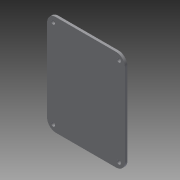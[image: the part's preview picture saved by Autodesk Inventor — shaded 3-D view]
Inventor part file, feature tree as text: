
AUTODESK INVENTOR PART (.ipt)
format: ipt  version: 2014 (Build 180170000, 170)  size: 131,584 bytes
history: native  units: mm
features: extrude x2, sketch x2, chamfer x1
ambient origin geometry x8: Origin, YZ Plane, XZ Plane, XY Plane, X Axis, Y Axis, Z Axis, Center Point
bodies: Solid1 (feature_tree)
feature tree (5):
  extrude  "Extrusion1"  Depth=5.0mm TaperAngle=0.0deg
  extrude  "Extrusion2"  Depth=5.0mm TaperAngle=45.0deg
  chamfer  "Chamfer1"  Distance=12.0mm
  sketch  "Sketch1"  dims[d0=2.2mm d1=0.0mm]
  sketch  "Sketch2"  dims[d5=2.5mm d6=6.0mm d7=2.5mm d8=6.0mm d9=2.5mm d10=6.0mm d11=2.5mm d12=6.0mm d14=5.0mm d15=0.0mm d16=2.0mm d17=2.0mm d18=45.0deg d21=12.0mm d22=12.0mm d23=18.0mm d24=18.0mm]
